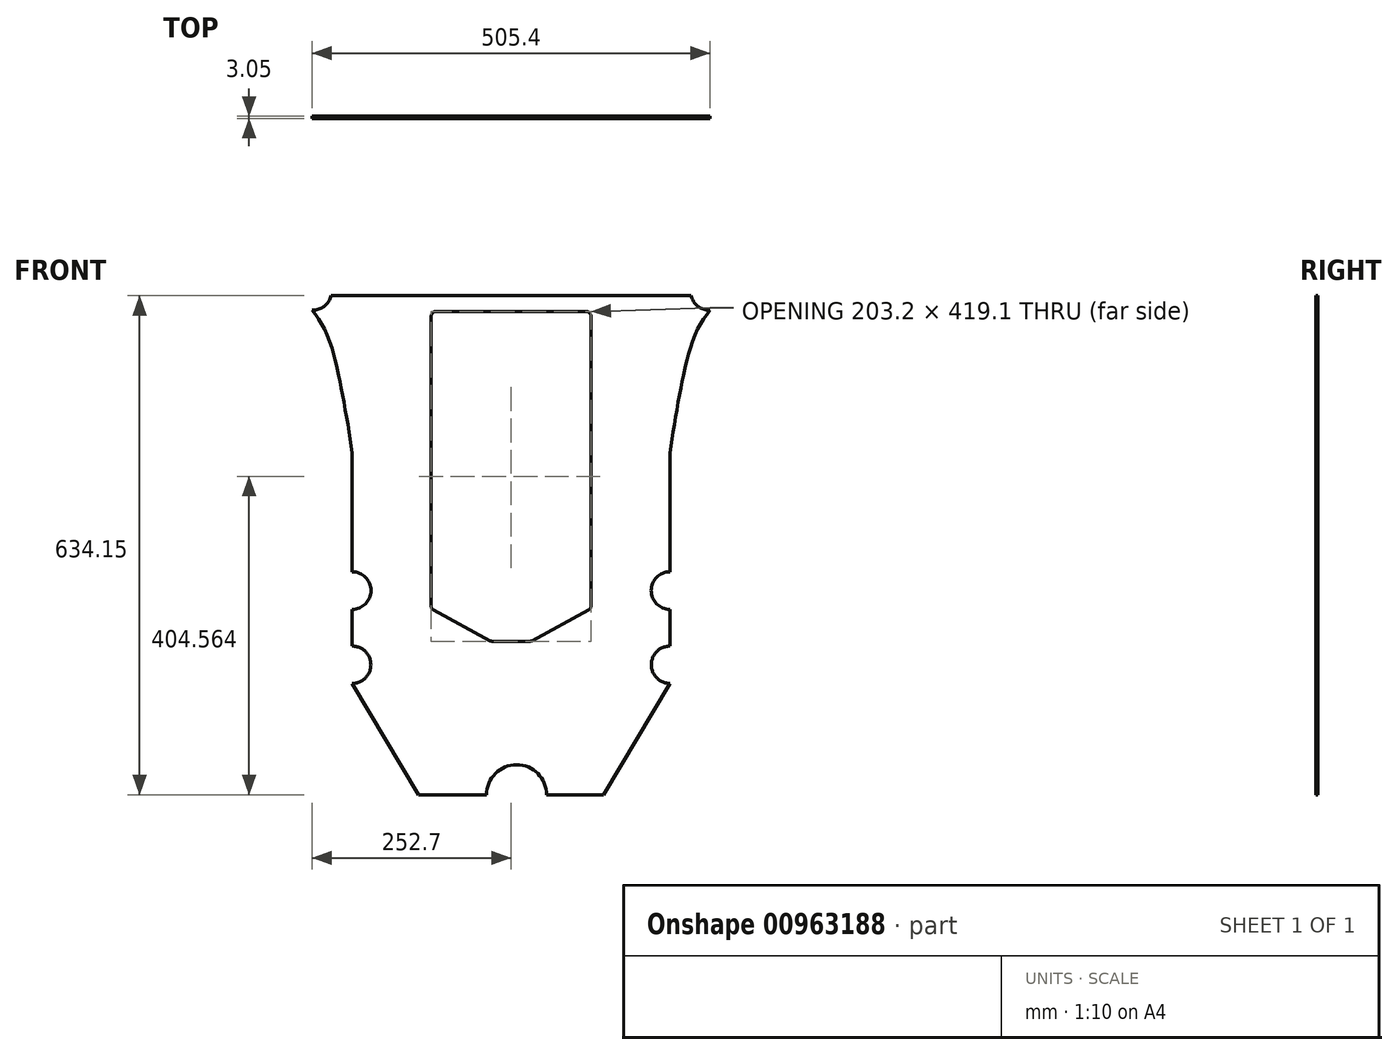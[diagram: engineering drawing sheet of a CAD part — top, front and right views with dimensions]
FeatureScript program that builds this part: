
annotation { "Feature Type Name" : "Feature", "Feature Type Description" : "" }
export const myFeature = defineFeature(function(context is Context, id is Id, definition is map)
    precondition{}
    {
        {
            var Q0;
            Q0=qCreatedBy(makeId("Front.planeOp"),FACE);
            var sketch = newSketch(context, id + "F0", { "sketchPlane" : qUnion([Q0])});
            skPoint(sketch, "E0.orphan", {"position": v(0, 374.32) * mm});
            skLineSegment(sketch, "E1", {"start": v(-101.6, 219.87) * mm, "end": v(-101.6, -147.74) * mm});
            skLineSegment(sketch, "E2", {"start": v(-95.25, 226.22) * mm, "end": v(95.25, 226.22) * mm});
            skLineSegment(sketch, "E3", {"start": v(23.35, -192.88) * mm, "end": v(-23.35, -192.88) * mm});
            skLineSegment(sketch, "E4", {"start": v(-98.26, -153.33) * mm, "end": v(-26.37, -192.11) * mm});
            skLineSegment(sketch, "E5", {"start": v(0, 268.15) * mm, "end": v(0, -423.16) * mm, "construction": true});
            skPoint(sketch, "E5.startSnap0", {"position": v(0, 226.22) * mm});
            skLineSegment(sketch, "E6.MirrorCS", {"start": v(98.26, -153.33) * mm, "end": v(26.37, -192.11) * mm});
            skPoint(sketch, "E7.orphan", {"position": v(-101.6, -192.88) * mm});
            skPoint(sketch, "E8.end.orphan", {"position": v(101.6, -192.88) * mm});
            skLineSegment(sketch, "E9", {"start": v(0, 246.26) * mm, "end": v(-228.6, 246.26) * mm});
            skLineSegment(sketch, "E10.MirrorCS", {"start": v(0, 246.26) * mm, "end": v(228.6, 246.26) * mm});
            skLineSegment(sketch, "E11", {"start": v(-117.35, -387.89) * mm, "end": v(-31.03, -387.89) * mm});
            skLineSegment(sketch, "E12.MirrorCS", {"start": v(117.35, -387.89) * mm, "end": v(45.17, -387.89) * mm});
            skLineSegment(sketch, "E13", {"start": v(-201.85, -198.24) * mm, "end": v(-201.85, -152.27) * mm});
            skLineSegment(sketch, "E14.MirrorCS", {"start": v(201.85, -198.24) * mm, "end": v(201.85, -152.27) * mm});
            skLineSegment(sketch, "E15", {"start": v(-117.35, -387.89) * mm, "end": v(-201.85, -246.4) * mm});
            skLineSegment(sketch, "E16.MirrorCS", {"start": v(117.35, -387.89) * mm, "end": v(201.85, -246.4) * mm});
            skArc(sketch, "E17", {"start": v(-201.85, -152.27) * mm, "mid": v(-177.97, -128.4) * mm, "end": v(-201.85, -104.52) * mm});
            skArc(sketch, "E18.MirrorC", {"start": v(201.85, -152.27) * mm, "mid": v(177.97, -128.4) * mm, "end": v(201.85, -104.52) * mm});
            skArc(sketch, "E19", {"start": v(-201.86, -246.38) * mm, "mid": v(-178.12, -222.66) * mm, "end": v(-201.85, -198.93) * mm});
            skArc(sketch, "E20.MirrorC", {"start": v(201.9, -246.38) * mm, "mid": v(178.12, -222.68) * mm, "end": v(201.85, -198.93) * mm});
            skLineSegment(sketch, "E21", {"start": v(-201.85, -198.24) * mm, "end": v(-201.85, -198.93) * mm});
            skLineSegment(sketch, "E22", {"start": v(201.85, -198.24) * mm, "end": v(201.85, -198.93) * mm});
            skLineSegment(sketch, "E23", {"start": v(101.6, 219.87) * mm, "end": v(101.6, -147.74) * mm});
            skArc(sketch, "E24", {"start": v(-252.7, 227.67) * mm, "mid": v(-237.35, 232.68) * mm, "end": v(-228.6, 246.26) * mm});
            skArc(sketch, "E25.MirrorCS", {"start": v(252.7, 227.67) * mm, "mid": v(237.35, 232.68) * mm, "end": v(228.6, 246.26) * mm});
            skFitSpline(sketch, "E26", {"points": [v(-201.85, 46.36) * mm, v(-209.18, 93.5) * mm, v(-217.88, 139.91) * mm, v(-223.69, 166.02) * mm, v(-236.74, 203.01) * mm, v(-252.7, 227.67) * mm], "startDerivative": vector(-30, 204.66) * mm, "endDerivative": vector(-94.57, 126.16) * mm});
            skFitSpline(sketch, "E27.MirrorCS", {"points": [v(201.85, 46.36) * mm, v(209.18, 93.5) * mm, v(217.88, 139.91) * mm, v(223.69, 166.02) * mm, v(236.74, 203.01) * mm, v(252.7, 227.67) * mm], "startDerivative": vector(30, 204.66) * mm, "endDerivative": vector(94.57, 126.16) * mm});
            skPoint(sketch, "E28.orphan", {"position": v(-201.85, 246.26) * mm});
            skPoint(sketch, "E29.orphan", {"position": v(201.85, 246.26) * mm});
            skLineSegment(sketch, "E30.trimOffspring", {"start": v(201.85, -104.52) * mm, "end": v(201.85, 46.36) * mm});
            skLineSegment(sketch, "E31", {"start": v(-201.85, -246.4) * mm, "end": v(-201.86, -246.38) * mm});
            skLineSegment(sketch, "E32", {"start": v(201.85, -246.4) * mm, "end": v(201.9, -246.38) * mm});
            skArc(sketch, "E33", {"start": v(45.17, -387.89) * mm, "mid": v(7.07, -349.79) * mm, "end": v(-31.03, -387.89) * mm});
            skPoint(sketch, "E34.orphan", {"position": v(0, -387.89) * mm});
            skLineSegment(sketch, "E35.trimOffspring", {"start": v(-201.85, -104.52) * mm, "end": v(-201.85, 46.36) * mm});
            skPoint(sketch, "E36.visualSharp", {"position": v(-101.6, 226.22) * mm});
            skArc(sketch, "E36.filletArc", {"start": v(-95.25, 226.22) * mm, "mid": v(-99.74, 224.36) * mm, "end": v(-101.6, 219.87) * mm});
            skPoint(sketch, "E37.visualSharp", {"position": v(101.6, 226.22) * mm});
            skArc(sketch, "E37.filletArc", {"start": v(101.6, 219.87) * mm, "mid": v(99.74, 224.36) * mm, "end": v(95.25, 226.22) * mm});
            skPoint(sketch, "E38.visualSharp", {"position": v(-101.6, -151.53) * mm});
            skArc(sketch, "E38.filletArc", {"start": v(-101.6, -147.74) * mm, "mid": v(-100.7, -151) * mm, "end": v(-98.26, -153.33) * mm});
            skPoint(sketch, "E39.visualSharp", {"position": v(-24.96, -192.88) * mm});
            skArc(sketch, "E39.filletArc", {"start": v(-26.37, -192.11) * mm, "mid": v(-24.9, -192.68) * mm, "end": v(-23.35, -192.88) * mm});
            skPoint(sketch, "E40.visualSharp", {"position": v(24.96, -192.88) * mm});
            skArc(sketch, "E40.filletArc", {"start": v(23.35, -192.88) * mm, "mid": v(24.9, -192.68) * mm, "end": v(26.37, -192.11) * mm});
            skPoint(sketch, "E41.visualSharp", {"position": v(101.6, -151.53) * mm});
            skArc(sketch, "E41.filletArc", {"start": v(98.26, -153.33) * mm, "mid": v(100.7, -151) * mm, "end": v(101.6, -147.74) * mm});
            skSolve(sketch);
        }
        {
            var Q0;
            Q0 = qSketchRegion(id + "F0", true);
            extrude(context, id + "F1", {"entities" : qUnion([Q0]), "depth" : 3.05 * mm, "offsetDistance" : 25.4 * mm});
        }
    });
